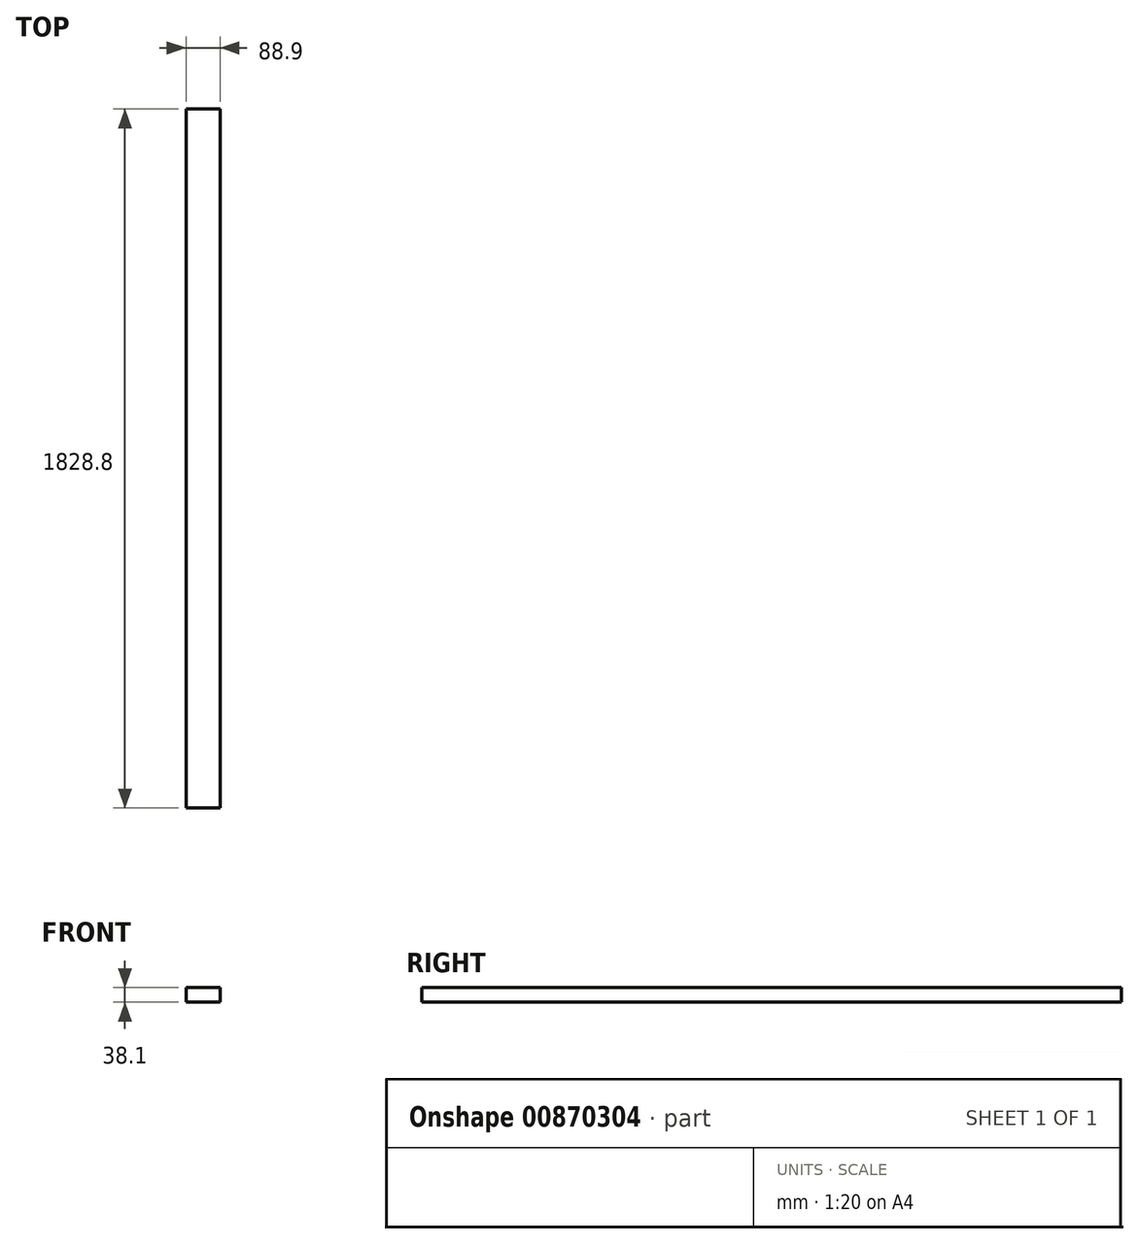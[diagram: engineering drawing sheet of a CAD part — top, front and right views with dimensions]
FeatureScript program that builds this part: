
annotation { "Feature Type Name" : "Feature", "Feature Type Description" : "" }
export const myFeature = defineFeature(function(context is Context, id is Id, definition is map)
    precondition{}
    {
        {
            var Q0;
            Q0=qCreatedBy(makeId("Front.planeOp"),FACE);
            var sketch = newSketch(context, id + "F0", { "sketchPlane" : qUnion([Q0])});
            skLineSegment(sketch, "E0.bottom", {"start": v(0, 0) * mm, "end": v(88.9, 0) * mm});
            skLineSegment(sketch, "E0.top", {"start": v(0, 38.1) * mm, "end": v(88.9, 38.1) * mm});
            skLineSegment(sketch, "E0.left", {"start": v(0, 0) * mm, "end": v(0, 38.1) * mm});
            skLineSegment(sketch, "E0.right", {"start": v(88.9, 0) * mm, "end": v(88.9, 38.1) * mm});
            skSolve(sketch);
        }
        {
            var Q0;
            Q0=makeQuery(id+"F0.imprint","IMPRINT",FACE,{"disambiguationData":[TD([[makeQuery(id+"F0.imprint","IMPRINT",EDGE,{"derivedFrom":sQuery(id+"F0.wireOp",EDGE,"E0.bottom")}),1.0]])]});
            extrude(context, id + "F1", {"entities" : qUnion([Q0]), "depth" : 1828.8 * mm, "offsetDistance" : 25.4 * mm});
        }
    });
